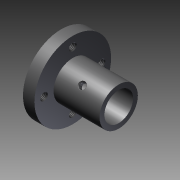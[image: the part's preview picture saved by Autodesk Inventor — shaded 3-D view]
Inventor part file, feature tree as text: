
AUTODESK INVENTOR PART (.ipt)
format: ipt  version: 2016 (Build 200138000, 138)  size: 176,640 bytes
history: native  units: mm
features: revolve x7, sketch x7, thread x6
ambient origin geometry x8: Origin, YZ Plane, XZ Plane, XY Plane, X Axis, Y Axis, Z Axis, Center Point
bodies: Solid1 (feature_tree)
feature tree (20):
  revolve  "Revolution1"  Angle=360.0deg
  revolve  "Revolution2"  Angle=360.0deg
  thread  "Thread1"  [1 undecoded]
  revolve  "Revolution3"  [1 undecoded]
  thread  "Thread2"  [1 undecoded]
  revolve  "Revolution4"  Angle=360.0deg
  thread  "Thread3"  [1 undecoded]
  revolve  "Revolution5"  [1 undecoded]
  thread  "Thread4"  [1 undecoded]
  revolve  "Revolution6"  [1 undecoded]
  thread  "Thread5"  [1 undecoded]
  revolve  "Revolution7"  [1 undecoded]
  thread  "Thread6"  [1 undecoded]
  sketch  "Sketch_1"  dims[d0=360.0deg d1=360.0deg]
  sketch  "Sketch_3"  dims[d7=360.0deg d8=5.242mm d9=0.0mm d10=360.0deg]
  sketch  "Sketch_2"  dims[d2=2.621mm d3=0.0mm d4=360.0deg d5=2.621mm d6=0.0mm]
  sketch  "Sketch_4"  dims[d11=5.242mm d12=0.0mm d13=360.0deg d14=5.242mm d15=0.0mm]
  sketch  "Sketch_9"  dims[d16=360.0deg d17=5.242mm d18=0.0mm]
  sketch  "Sketch_10"
  sketch  "Sketch_11"
note: 10 required parameter values undecoded (feature->parameter linkage not recoverable at this tier; creation-order binding heuristic only, values carry confidence <= 0.55)